# Revit family: Gira_128700
name_source: partatom
category: Elektroinstallationen
revit_build: Autodesk Revit 2017 (Build: 20160225_1515(x64)
units: mm (PartAtom-declared; Revit-internal decimal feet)

## family parameters
Basisbauteil = Fläche
Beim Laden mit Abzugskörper schneiden = Nein
Bemaßung runder Anschluss = Durchmesser verwenden
Beschriftungsausrichtung beibehalten = Nein
Gemeinsam genutzt = Nein
Raumberechnungspunkt = Nein
Teiletyp = Normal

## types (1)
- Steuergerät Audio REG Türko
    Anwendung = sonstige
    Anzahl der anschließbaren Teilnehmer = 70
    Ausgangsspannung [Volt] = 12
    Auswertefunktion = Nein
    BIM = https://media.live.bim.site 00_REG 6.rfa
    BIMSITE_PRODUCT_ID = 2c913e152b33b86ff14d9ba59fdf835af8299b99
    Beschreibung = Steuergerät Audio  REG Merkmale:  Steuergerät zur Versorgung der Audiokomponenten des Gira Türkommunikationsbusses.  Versorgung des verpolungssicheren und kurzschlussfesten 2-Draht-Busses.  Selbstrückstellende elektronische Kurzschluss- und Überlasterkennung der Betriebsspannungen und des Busanschlusses.  Tasten für System- und Türöffnerprogrammierung.  LED-Statusanzeigen für Betrieb, Überlast, Systemprogrammierung und Türöffnerprogrammierung.  AC 12 V Ausgang zur Spannungsversorgung eines handelsüblichen Türöffners.  Permanenter AC 12 V Ausgang zur Spannungsversorgung eines TKS-TK-Gateways.  Relaisausgang zum Schalten eines Türöffners mit eigener Spannungsversorgung.  Türöffnerschaltzeit stufenlos von 1 bis 10 s einstellbar.  Hinweise :  Das Steuergerät Audio ist für den Einbau in die Unterverteilung vorgesehen. Ist dies nicht möglich, handelsüblichen Aufputzverteiler verwenden.  Mit dieser Komponente ist der Aufbau von Türkommunikationsanlagen mit bis zu 70 Teilnehmern möglich (z. B. 1 x Einbaulautsprecher, 5 x Erweiterungsmodul für Einbaulautsprecher, 68 x Wohnungsstation AP).
    Datenblatt = https://media.live.bim.site
    Datenblatt 1 = https://media.live.bim.site
    Eingangsspannung [Volt] = 230
    GTIN = 4010337287001
    HAN = 128700
    HeinzeBIM = https://www.heinze.de
    Hersteller = Gira
    Installationstechnik = Bus-System
    Integrierte Türöffnerschaltung = Ja
    Ist System = Nein
    Ist Zubehör = Nein
    Kosten = 0 $
    Produktseite = https://media.live.bim.site
    Programmiersperre = Nein
    Schutzart (IP) = IP20
    Serviceanzeigen = Ja
    Steuerfunktion = Ja
    Stromart = AC
    Typname = Steuergerät Audio REG Türko
    URL = https://www.gira.de
    Vorgabe-Ansicht = 1219 mm

## geometry (parser evidence)
native form markers: Sweep x1
no freeform markers — native parametric forms only
